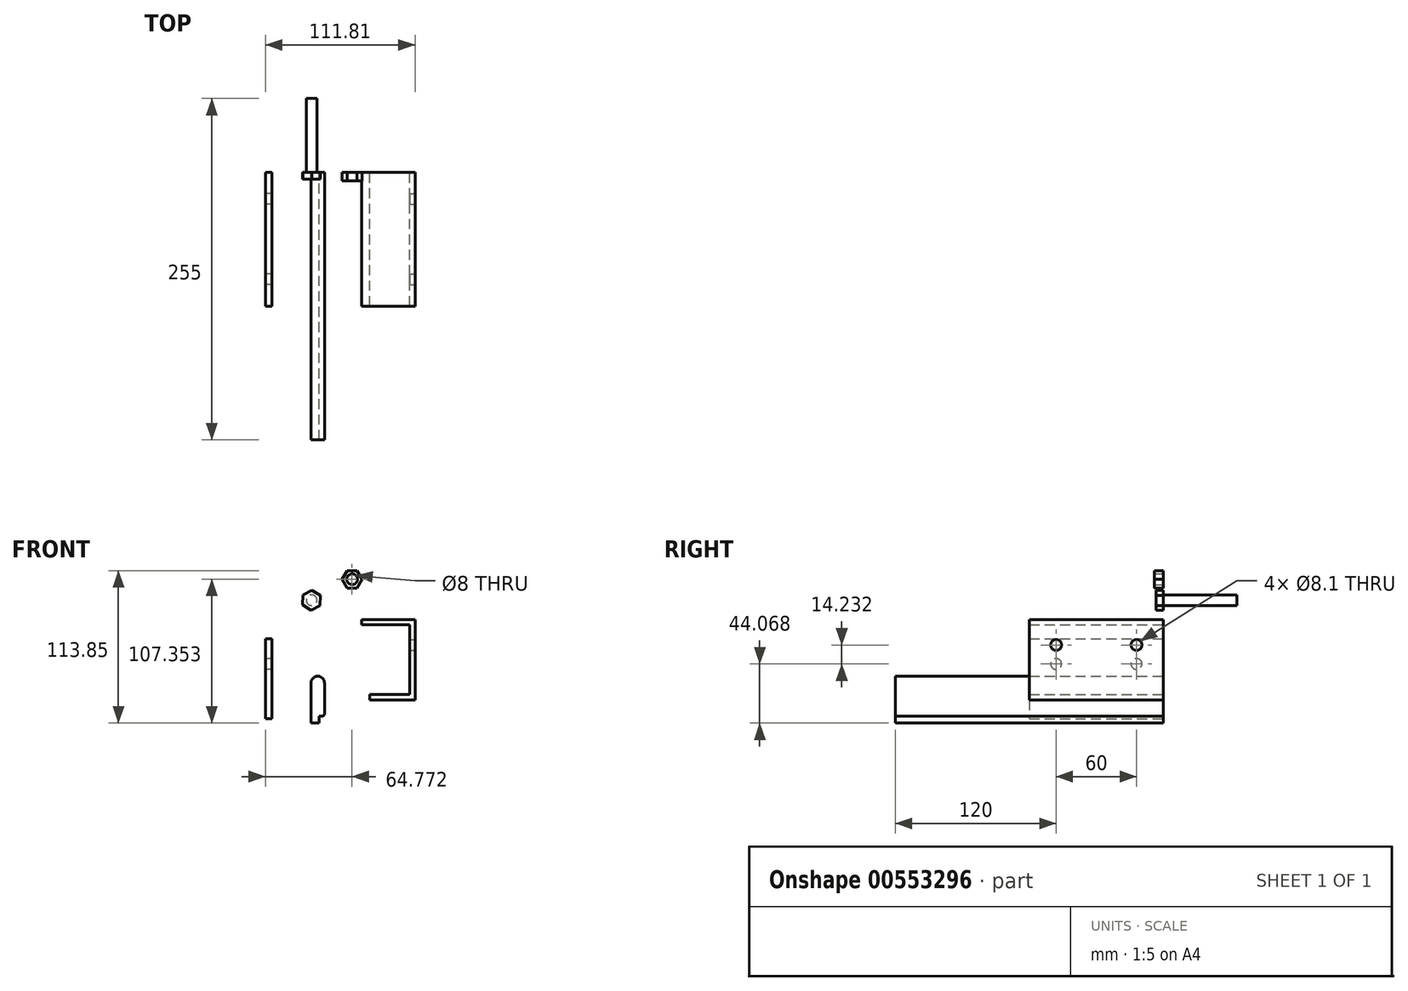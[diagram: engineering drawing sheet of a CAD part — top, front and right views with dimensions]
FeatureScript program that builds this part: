
annotation { "Feature Type Name" : "Feature", "Feature Type Description" : "" }
export const myFeature = defineFeature(function(context is Context, id is Id, definition is map)
    precondition{}
    {
        {
            var Q0;
            Q0=qCreatedBy(makeId("Front.planeOp"),FACE);
            var sketch = newSketch(context, id + "F0", { "sketchPlane" : qUnion([Q0])});
            skLineSegment(sketch, "E0.bottom", {"start": v(-89.55, 12.1) * mm, "end": v(-84.55, 12.1) * mm});
            skLineSegment(sketch, "E0.top", {"start": v(-89.55, -47.9) * mm, "end": v(-84.55, -47.9) * mm});
            skLineSegment(sketch, "E0.left", {"start": v(-89.55, 12.1) * mm, "end": v(-89.55, -47.9) * mm});
            skLineSegment(sketch, "E0.right", {"start": v(-84.55, 12.1) * mm, "end": v(-84.55, -47.9) * mm});
            skSolve(sketch);
        }
        {
            var Q0;
            Q0 = qSketchRegion(id + "F0", true);
            extrude(context, id + "F1", {"entities" : qUnion([Q0]), "depth" : 100 * mm, "offsetDistance" : 25 * mm});
        }
        {
            var Q0;
            Q0=qCreatedBy(makeId("Front.planeOp"),FACE);
            var sketch = newSketch(context, id + "F2", { "sketchPlane" : qUnion([Q0])});
            skLineSegment(sketch, "E1", {"start": v(-17.74, 26.34) * mm, "end": v(22.26, 26.34) * mm});
            skLineSegment(sketch, "E2", {"start": v(22.26, 26.34) * mm, "end": v(22.26, -33.66) * mm});
            skLineSegment(sketch, "E3", {"start": v(22.26, -33.66) * mm, "end": v(-11.74, -33.66) * mm});
            skLineSegment(sketch, "E4", {"start": v(-11.74, -33.66) * mm, "end": v(-11.74, -29.66) * mm});
            skLineSegment(sketch, "E5", {"start": v(-11.74, -29.66) * mm, "end": v(18.26, -29.66) * mm});
            skLineSegment(sketch, "E6", {"start": v(18.26, -29.66) * mm, "end": v(18.26, 22.34) * mm});
            skLineSegment(sketch, "E7", {"start": v(-17.74, 26.34) * mm, "end": v(-17.74, 22.34) * mm});
            skLineSegment(sketch, "E8", {"start": v(-17.74, 22.34) * mm, "end": v(18.26, 22.34) * mm});
            skSolve(sketch);
        }
        {
            var Q0;
            Q0 = qSketchRegion(id + "F2", true);
            extrude(context, id + "F3", {"entities" : qUnion([Q0]), "depth" : 100 * mm, "offsetDistance" : 25 * mm});
        }
        {
            var Q0;
            Q0=makeQuery(id+"F3.opExtrude","SWEPT_FACE",FACE,{"disambiguationData":[OSD([sQuery(id+"F2.wireOp",EDGE,"E2")])]});
            var sketch = newSketch(context, id + "F4", { "sketchPlane" : qUnion([Q0])});
            skCircle(sketch, "E9", {"center": v(-20, 7.34) * mm, "radius": 4.05 * mm});
            skCircle(sketch, "E10", {"center": v(-80, 7.34) * mm, "radius": 4.05 * mm});
            skSolve(sketch);
        }
        {
            var Q0;
            Q0 = qSketchRegion(id + "F4", true);
            extrude(context, id + "F5", {"entities" : qUnion([Q0]), "operationType" : NewBodyOperationType.REMOVE, "oppositeDirection" : true, "depth" : 4 * mm, "offsetDistance" : 25 * mm});
        }
        {
            var Q0;
            Q0=makeQuery(id+"F1.opExtrude","SWEPT_FACE",FACE,{"disambiguationData":[OSD([sQuery(id+"F0.wireOp",EDGE,"E0.left")])]});
            var sketch = newSketch(context, id + "F6", { "sketchPlane" : qUnion([Q0])});
            skCircle(sketch, "E11", {"center": v(20, -6.9) * mm, "radius": 4.05 * mm});
            skCircle(sketch, "E12", {"center": v(80, -6.9) * mm, "radius": 4.05 * mm});
            skSolve(sketch);
        }
        {
            var Q0;
            Q0 = qSketchRegion(id + "F6", true);
            extrude(context, id + "F7", {"entities" : qUnion([Q0]), "operationType" : NewBodyOperationType.REMOVE, "oppositeDirection" : true, "depth" : 5 * mm, "offsetDistance" : 25 * mm});
        }
        {
            var Q0;
            Q0=qCreatedBy(makeId("Front.planeOp"),FACE);
            var sketch = newSketch(context, id + "F8", { "sketchPlane" : qUnion([Q0])});
            skArc(sketch, "E13", {"start": v(-45.4, -20.96) * mm, "mid": v(-50.4, -15.96) * mm, "end": v(-55.4, -20.96) * mm});
            skLineSegment(sketch, "E14.top", {"start": v(-49.4, -45.96) * mm, "end": v(-47.4, -45.96) * mm});
            skLineSegment(sketch, "E14.left", {"start": v(-55.4, -20.96) * mm, "end": v(-55.4, -45.96) * mm});
            skLineSegment(sketch, "E14.right", {"start": v(-45.4, -20.96) * mm, "end": v(-45.4, -43.96) * mm});
            skLineSegment(sketch, "E15.top", {"start": v(-55.4, -50.96) * mm, "end": v(-49.4, -50.96) * mm});
            skLineSegment(sketch, "E15.left", {"start": v(-55.4, -45.96) * mm, "end": v(-55.4, -50.96) * mm});
            skLineSegment(sketch, "E15.right", {"start": v(-49.4, -45.96) * mm, "end": v(-49.4, -50.96) * mm});
            skArc(sketch, "E16", {"start": v(-47.4, -45.96) * mm, "mid": v(-45.99, -45.37) * mm, "end": v(-45.4, -43.96) * mm});
            skSolve(sketch);
        }
        {
            var Q0;
            Q0 = qSketchRegion(id + "F8", true);
            extrude(context, id + "F9", {"entities" : qUnion([Q0]), "depth" : 200 * mm, "offsetDistance" : 25 * mm});
        }
        {
            var Q0;
            Q0=qCreatedBy(makeId("Front.planeOp"),FACE);
            var sketch = newSketch(context, id + "F10", { "sketchPlane" : qUnion([Q0])});
            skCircle(sketch, "E17.cCircle", {"center": v(-55.02, 40.8) * mm, "radius": 6.5 * mm, "construction": true});
            skLineSegment(sketch, "E17.0", {"start": v(-48.67, 36.8) * mm, "end": v(-55.3, 33.3) * mm});
            skLineSegment(sketch, "E17.1", {"start": v(-55.3, 33.3) * mm, "end": v(-61.66, 37.3) * mm});
            skLineSegment(sketch, "E17.2", {"start": v(-61.66, 37.3) * mm, "end": v(-61.38, 44.8) * mm});
            skLineSegment(sketch, "E17.3", {"start": v(-61.38, 44.8) * mm, "end": v(-54.74, 48.3) * mm});
            skLineSegment(sketch, "E17.4", {"start": v(-54.74, 48.3) * mm, "end": v(-48.39, 44.3) * mm});
            skLineSegment(sketch, "E17.5", {"start": v(-48.39, 44.3) * mm, "end": v(-48.67, 36.8) * mm});
            skPoint(sketch, "E17.0.midPoint", {"position": v(-51.99, 35.06) * mm});
            skSolve(sketch);
        }
        {
            var Q0;
            Q0 = qSketchRegion(id + "F10", true);
            extrude(context, id + "F11", {"entities" : qUnion([Q0]), "depth" : 5.3 * mm, "offsetDistance" : 25 * mm});
        }
        {
            var Q0;
            Q0=makeQuery(id+"F11.opExtrude","CAP_FACE",FACE,{"disambiguationData":[OSD([sQuery(id+"F10.wireOp",EDGE,"E17.0"),sQuery(id+"F10.wireOp",EDGE,"E17.1"),sQuery(id+"F10.wireOp",EDGE,"E17.2"),sQuery(id+"F10.wireOp",EDGE,"E17.3"),sQuery(id+"F10.wireOp",EDGE,"E17.4"),sQuery(id+"F10.wireOp",EDGE,"E17.5")])],"isStart":true});
            var sketch = newSketch(context, id + "F12", { "sketchPlane" : qUnion([Q0])});
            skCircle(sketch, "E18", {"center": v(55.02, 40.8) * mm, "radius": 4 * mm});
            skSolve(sketch);
        }
        {
            var Q0;
            Q0 = qSketchRegion(id + "F12", true);
            extrude(context, id + "F13", {"entities" : qUnion([Q0]), "operationType" : NewBodyOperationType.ADD, "depth" : 55 * mm, "offsetDistance" : 25 * mm});
        }
        {
            var Q0;
            Q0=qCreatedBy(makeId("Front.planeOp"),FACE);
            var sketch = newSketch(context, id + "F14", { "sketchPlane" : qUnion([Q0])});
            skCircle(sketch, "E19.cCircle", {"center": v(-24.78, 56.4) * mm, "radius": 6.5 * mm, "construction": true});
            skLineSegment(sketch, "E19.0", {"start": v(-21.02, 49.9) * mm, "end": v(-28.53, 49.9) * mm});
            skLineSegment(sketch, "E19.1", {"start": v(-28.53, 49.9) * mm, "end": v(-32.28, 56.4) * mm});
            skLineSegment(sketch, "E19.2", {"start": v(-32.28, 56.4) * mm, "end": v(-28.53, 62.9) * mm});
            skLineSegment(sketch, "E19.3", {"start": v(-28.53, 62.9) * mm, "end": v(-21.02, 62.9) * mm});
            skLineSegment(sketch, "E19.4", {"start": v(-21.02, 62.9) * mm, "end": v(-17.27, 56.4) * mm});
            skLineSegment(sketch, "E19.5", {"start": v(-17.27, 56.4) * mm, "end": v(-21.02, 49.9) * mm});
            skPoint(sketch, "E19.0.midPoint", {"position": v(-24.78, 49.9) * mm});
            skCircle(sketch, "E20", {"center": v(-24.78, 56.4) * mm, "radius": 4 * mm});
            skSolve(sketch);
        }
        {
            var Q0;
            Q0 = qSketchRegion(id + "F14", true);
            extrude(context, id + "F15", {"entities" : qUnion([Q0]), "depth" : 6.5 * mm, "offsetDistance" : 25 * mm});
        }
    });
